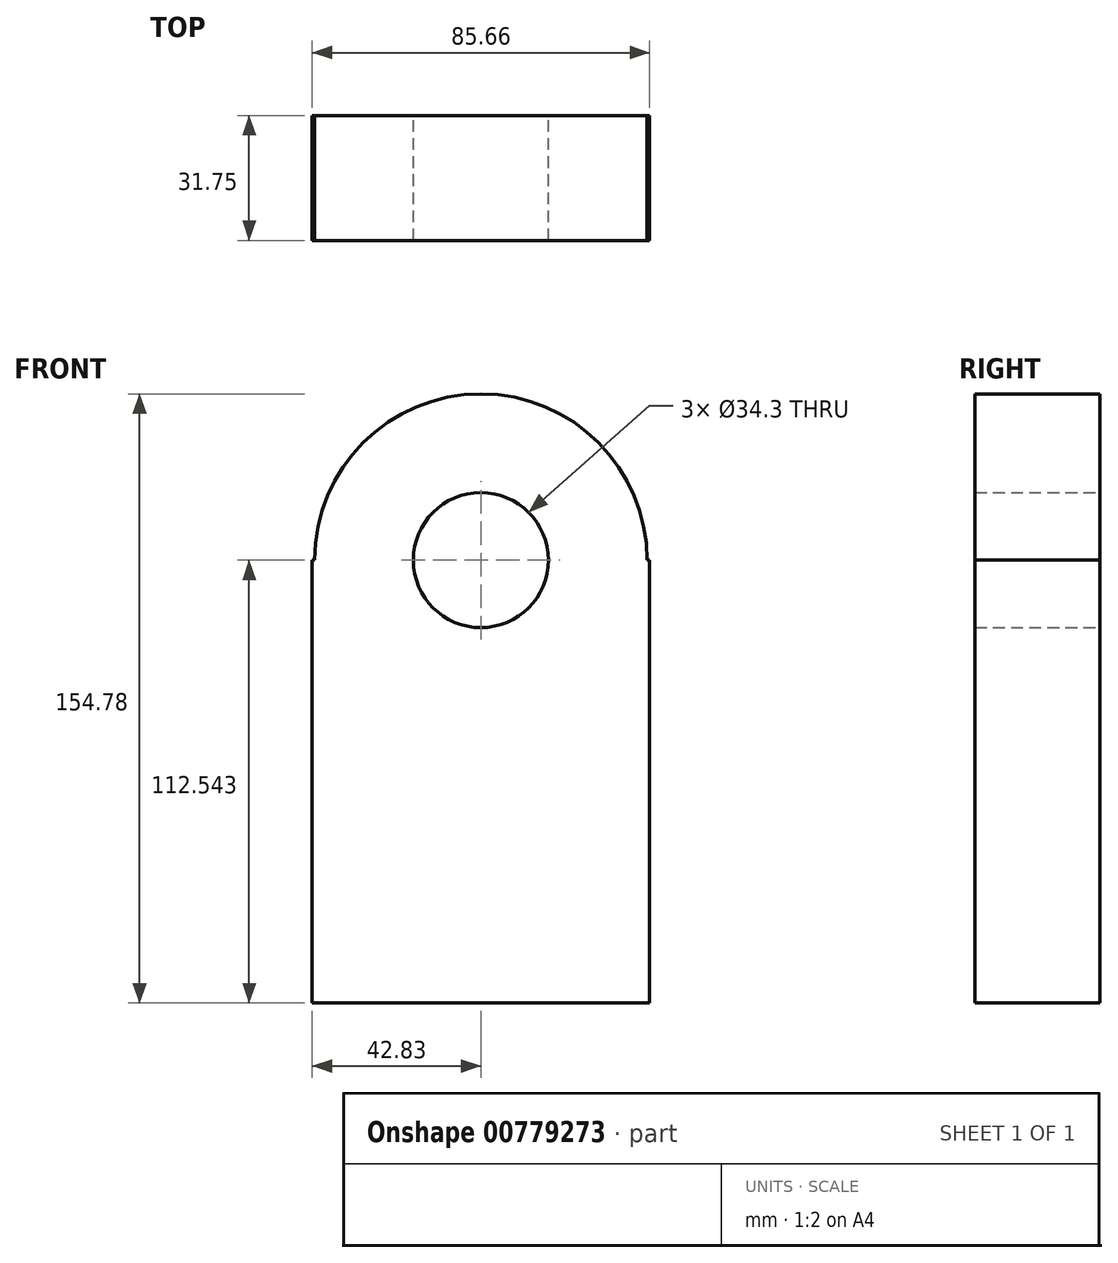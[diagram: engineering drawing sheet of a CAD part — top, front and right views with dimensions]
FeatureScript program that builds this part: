
annotation { "Feature Type Name" : "Feature", "Feature Type Description" : "" }
export const myFeature = defineFeature(function(context is Context, id is Id, definition is map)
    precondition{}
    {
        {
            var Q0;
            Q0=qCreatedBy(makeId("Front.planeOp"),FACE);
            var sketch = newSketch(context, id + "F0", { "sketchPlane" : qUnion([Q0])});
            skLineSegment(sketch, "E0.bottom", {"start": v(-42.83, 56.27) * mm, "end": v(42.83, 56.27) * mm});
            skLineSegment(sketch, "E0.top", {"start": v(-42.83, -56.27) * mm, "end": v(42.83, -56.27) * mm});
            skLineSegment(sketch, "E0.left", {"start": v(-42.83, 56.27) * mm, "end": v(-42.83, -56.27) * mm});
            skLineSegment(sketch, "E0.right", {"start": v(42.83, 56.27) * mm, "end": v(42.83, -56.27) * mm});
            skPoint(sketch, "E0.middle", {"position": v(0, 0) * mm});
            skCircle(sketch, "E1", {"center": v(0, 56.27) * mm, "radius": 42.24 * mm});
            skCircle(sketch, "E2", {"center": v(0, 56.27) * mm, "radius": 17.15 * mm});
            skSolve(sketch);
        }
        {
            var Q0;
            Q0=makeQuery(id+"F0.imprint","IMPRINT",FACE,{"disambiguationData":[TD([[makeQuery(id+"F0.imprint","IMPRINT",EDGE,{"derivedFrom":sQuery(id+"F0.wireOp",EDGE,"E0.top")}),1.0]])]});
            var Q1;
            {var subQ0=sQuery(id+"F0.wireOp",EDGE,"E1");var subQ1=sQuery(id+"F0.wireOp",EDGE,"E0.bottom");var subQ2=makeQuery(id+"F0.imprint","INTERSECT",VERTEX,{"disambiguationData":[OD(0.0)],"derivedFrom":[subQ1,subQ0]});Q1=makeQuery(id+"F0.imprint","IMPRINT",FACE,{"disambiguationData":[TD([[makeQuery(id+"F0.imprint","IMPRINT",EDGE,{"disambiguationData":[TD([[subQ2,-1.0]])],"derivedFrom":subQ1}),-1.0]])]});}
            var Q2;
            {var subQ0=sQuery(id+"F0.wireOp",EDGE,"E1");var subQ1=sQuery(id+"F0.wireOp",EDGE,"E0.bottom");var subQ2=makeQuery(id+"F0.imprint","INTERSECT",VERTEX,{"disambiguationData":[OD(0.0)],"derivedFrom":[subQ1,subQ0]});Q2=makeQuery(id+"F0.imprint","IMPRINT",FACE,{"disambiguationData":[TD([[makeQuery(id+"F0.imprint","IMPRINT",EDGE,{"disambiguationData":[TD([[subQ2,-1.0]])],"derivedFrom":subQ1}),1.0]])]});}
            extrude(context, id + "F1", {"entities" : qUnion([Q0, Q1, Q2]), "depth" : 31.75 * mm, "offsetDistance" : 25.4 * mm});
        }
    });
